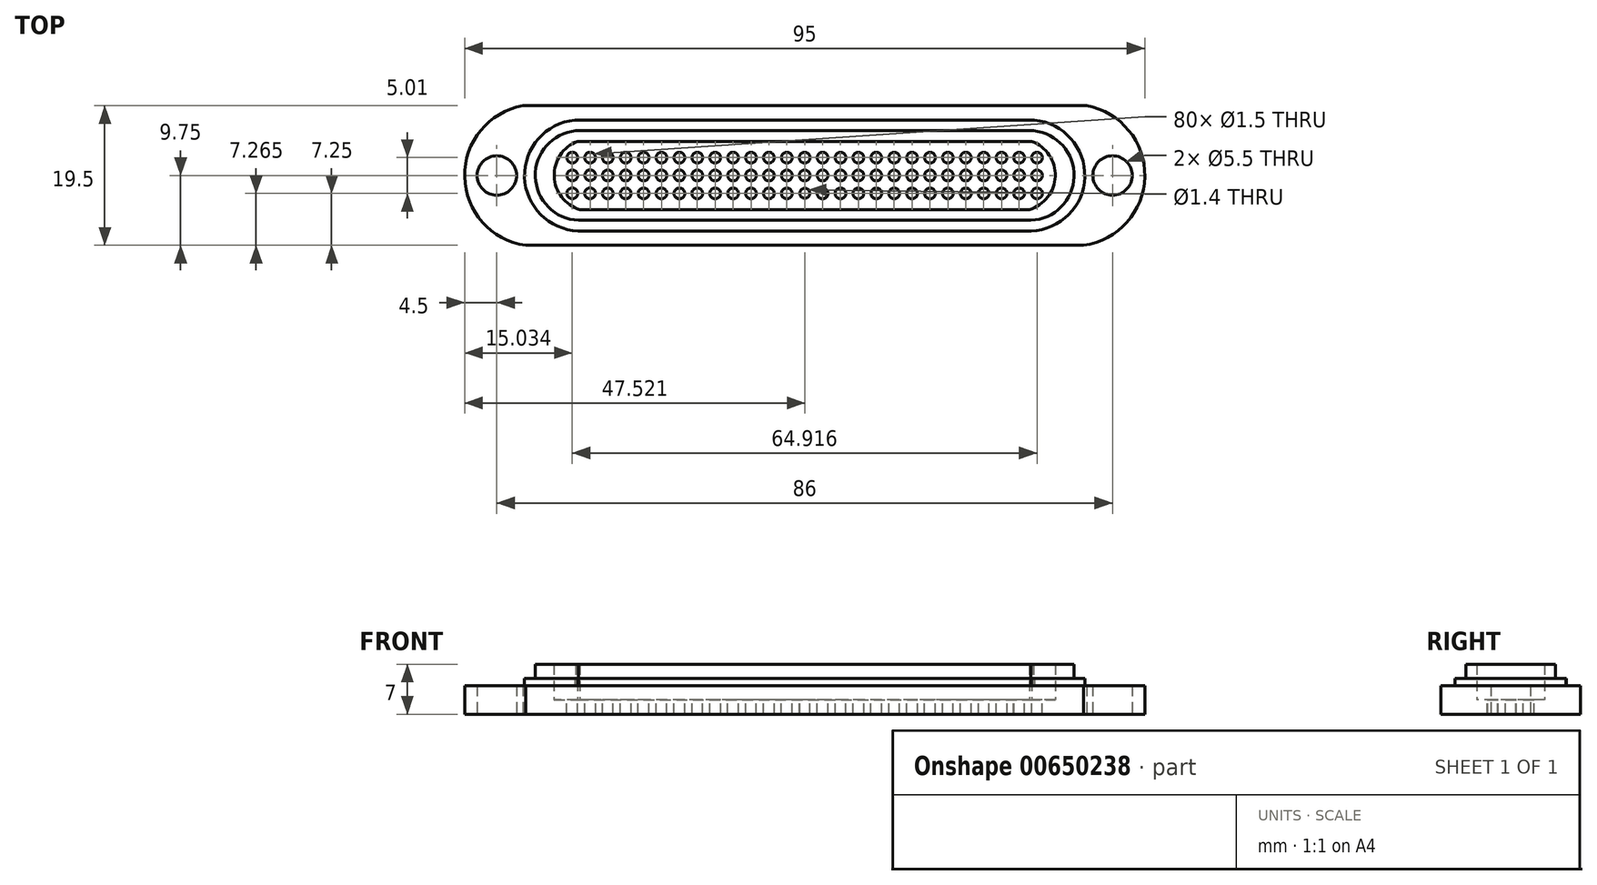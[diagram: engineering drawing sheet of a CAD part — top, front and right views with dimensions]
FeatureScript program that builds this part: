
annotation { "Feature Type Name" : "Feature", "Feature Type Description" : "" }
export const myFeature = defineFeature(function(context is Context, id is Id, definition is map)
    precondition{}
    {
        {
            var Q0;
            Q0=qCreatedBy(makeId("Top.planeOp"),FACE);
            var sketch = newSketch(context, id + "F0", { "sketchPlane" : qUnion([Q0])});
            skLineSegment(sketch, "E0.bottom", {"start": v(0, -9.75) * mm, "end": v(-38.98, -9.75) * mm});
            skLineSegment(sketch, "E0.top", {"start": v(0, 9.75) * mm, "end": v(-39.37, 9.75) * mm});
            skLineSegment(sketch, "E0.right", {"start": v(-47.5, 0) * mm, "end": v(-47.5, 0) * mm});
            skPoint(sketch, "E0.middle", {"position": v(0, 0) * mm});
            skArc(sketch, "E1", {"start": v(-39.37, 9.75) * mm, "mid": v(-47.5, -0.17) * mm, "end": v(-38.98, -9.75) * mm});
            skPoint(sketch, "E1.first.point", {"position": v(-38.98, -9.75) * mm});
            skPoint(sketch, "E1.second.point", {"position": v(-39.37, 9.75) * mm});
            skPoint(sketch, "E1.third.point", {"position": v(-47.5, 0) * mm});
            skLineSegment(sketch, "E2", {"start": v(0, 13.54) * mm, "end": v(0, -9.75) * mm, "construction": true});
            skPoint(sketch, "E3.orphan", {"position": v(-47.5, 9.75) * mm});
            skPoint(sketch, "E4.orphan", {"position": v(-47.5, -9.75) * mm});
            skPoint(sketch, "E0.left.end.orphan", {"position": v(47.5, 9.75) * mm});
            skPoint(sketch, "E0.left.start.orphan", {"position": v(47.5, -9.75) * mm});
            skLineSegment(sketch, "E5", {"start": v(-47.5, 0) * mm, "end": v(-43, 0) * mm, "construction": true});
            skCircle(sketch, "E6", {"center": v(-43, 0) * mm, "radius": 2.75 * mm});
            skLineSegment(sketch, "E7.MirrorCS", {"start": v(47.5, 0) * mm, "end": v(47.5, 0) * mm});
            skLineSegment(sketch, "E8.MirrorCS", {"start": v(47.5, 0) * mm, "end": v(43, 0) * mm, "construction": true});
            skPoint(sketch, "E9.MirrorP", {"position": v(39.37, 9.75) * mm});
            skArc(sketch, "E10.MirrorCS", {"start": v(39.37, 9.75) * mm, "mid": v(47.5, -0.17) * mm, "end": v(38.98, -9.75) * mm});
            skPoint(sketch, "E11.MirrorP", {"position": v(38.98, -9.75) * mm});
            skCircle(sketch, "E12.MirrorC", {"center": v(43, 0) * mm, "radius": 2.75 * mm});
            skPoint(sketch, "E13.MirrorP", {"position": v(47.5, 0) * mm});
            skLineSegment(sketch, "E14.MirrorCS", {"start": v(0, -9.75) * mm, "end": v(38.98, -9.75) * mm});
            skLineSegment(sketch, "E15.MirrorCS", {"start": v(0, 9.75) * mm, "end": v(39.37, 9.75) * mm});
            skLineSegment(sketch, "E16.0", {"start": v(-0.33, -6.25) * mm, "end": v(-31.59, -6.25) * mm});
            skLineSegment(sketch, "E16.2", {"start": v(-5.28, -6.25) * mm, "end": v(31.59, -6.25) * mm});
            skLineSegment(sketch, "E16.4", {"start": v(0, 6.25) * mm, "end": v(31.96, 6.25) * mm});
            skLineSegment(sketch, "E16.5", {"start": v(0, 6.25) * mm, "end": v(-31.96, 6.25) * mm});
            skLineSegment(sketch, "E17.0", {"start": v(-0.33, -4.75) * mm, "end": v(-31.39, -4.75) * mm});
            skArc(sketch, "E17.1", {"start": v(-31.71, 4.75) * mm, "mid": v(-35, -0.12) * mm, "end": v(-31.39, -4.75) * mm});
            skLineSegment(sketch, "E17.2", {"start": v(-5.28, -4.75) * mm, "end": v(31.39, -4.75) * mm});
            skArc(sketch, "E17.3", {"start": v(31.71, 4.75) * mm, "mid": v(35, -0.12) * mm, "end": v(31.39, -4.75) * mm});
            skLineSegment(sketch, "E17.4", {"start": v(0, 4.75) * mm, "end": v(31.71, 4.75) * mm});
            skLineSegment(sketch, "E17.5", {"start": v(0, 4.75) * mm, "end": v(-31.71, 4.75) * mm});
            skLineSegment(sketch, "E18", {"start": v(-0.33, -4.75) * mm, "end": v(-5.28, -4.75) * mm});
            skLineSegment(sketch, "E19", {"start": v(-5.28, -6.25) * mm, "end": v(-0.33, -6.25) * mm});
            skArc(sketch, "E20", {"start": v(-31.96, 6.25) * mm, "mid": v(-37.62, -0.17) * mm, "end": v(-31.59, -6.25) * mm});
            skArc(sketch, "E21", {"start": v(31.59, -6.25) * mm, "mid": v(37.62, -0.18) * mm, "end": v(31.96, 6.25) * mm});
            skArc(sketch, "E22.0", {"start": v(-32.1, 7.74) * mm, "mid": v(-39.12, -0.22) * mm, "end": v(-31.64, -7.75) * mm});
            skLineSegment(sketch, "E23.0", {"start": v(0, 7.75) * mm, "end": v(-31.96, 7.75) * mm});
            skLineSegment(sketch, "E24.0", {"start": v(-0.33, -7.75) * mm, "end": v(-31.59, -7.75) * mm});
            skLineSegment(sketch, "E25.MirrorCS", {"start": v(0, 7.75) * mm, "end": v(31.96, 7.75) * mm});
            skArc(sketch, "E26.MirrorCS", {"start": v(32.1, 7.74) * mm, "mid": v(39.12, -0.22) * mm, "end": v(31.64, -7.75) * mm});
            skLineSegment(sketch, "E27.MirrorCS", {"start": v(0.33, -7.75) * mm, "end": v(31.59, -7.75) * mm});
            skLineSegment(sketch, "E28", {"start": v(-0.33, -7.75) * mm, "end": v(0.33, -7.75) * mm});
            skLineSegment(sketch, "E29", {"start": v(-32.1, 7.74) * mm, "end": v(-31.96, 7.75) * mm});
            skLineSegment(sketch, "E30", {"start": v(-31.64, -7.75) * mm, "end": v(-31.59, -7.75) * mm});
            skLineSegment(sketch, "E31", {"start": v(31.59, -7.75) * mm, "end": v(31.64, -7.75) * mm});
            skLineSegment(sketch, "E32", {"start": v(31.96, 7.75) * mm, "end": v(32.1, 7.74) * mm});
            skSolve(sketch);
        }
        {
            var Q0;
            Q0 = qSketchRegion(id + "F0", true);
            extrude(context, id + "F1", {"entities" : qUnion([Q0]), "depth" : 4 * mm, "offsetDistance" : 25 * mm});
        }
        {
            var Q0;
            Q0=makeQuery(id+"F0.imprint","IMPRINT",FACE,{"disambiguationData":[TD([[makeQuery(id+"F0.imprint","IMPRINT",EDGE,{"derivedFrom":sQuery(id+"F0.wireOp",EDGE,"E16.0")}),1.0]])]});
            extrude(context, id + "F2", {"entities" : qUnion([Q0]), "operationType" : NewBodyOperationType.ADD, "depth" : 5 * mm, "offsetDistance" : 25 * mm});
        }
        {
            var Q0;
            Q0=makeQuery(id+"F0.imprint","IMPRINT",FACE,{"disambiguationData":[TD([[makeQuery(id+"F0.imprint","IMPRINT",EDGE,{"derivedFrom":sQuery(id+"F0.wireOp",EDGE,"E16.0")}),-1.0]])]});
            extrude(context, id + "F3", {"entities" : qUnion([Q0]), "operationType" : NewBodyOperationType.ADD, "depth" : 7 * mm, "offsetDistance" : 25 * mm});
        }
        {
            var Q0;
            Q0=makeQuery(id+"F0.imprint","IMPRINT",FACE,{"disambiguationData":[TD([[makeQuery(id+"F0.imprint","IMPRINT",EDGE,{"derivedFrom":sQuery(id+"F0.wireOp",EDGE,"E17.0")}),-1.0]])]});
            extrude(context, id + "F4", {"entities" : qUnion([Q0]), "operationType" : NewBodyOperationType.ADD, "depth" : 2 * mm, "offsetDistance" : 25 * mm});
        }
        {
            var Q0;
            Q0=makeQuery(id+"F4.opExtrude","CAP_FACE",FACE,{"disambiguationData":[OSD([sQuery(id+"F0.wireOp",EDGE,"E17.0"),sQuery(id+"F0.wireOp",EDGE,"E17.1"),sQuery(id+"F0.wireOp",EDGE,"E17.2"),sQuery(id+"F0.wireOp",EDGE,"E17.3"),sQuery(id+"F0.wireOp",EDGE,"E17.4"),sQuery(id+"F0.wireOp",EDGE,"E17.5"),sQuery(id+"F0.wireOp",EDGE,"E18")])],"isStart":false});
            var sketch = newSketch(context, id + "F5", { "sketchPlane" : qUnion([Q0])});
            skArc(sketch, "E33", {"start": v(0, -0.75) * mm, "mid": v(0.75, 0) * mm, "end": v(0, 0.75) * mm});
            skArc(sketch, "E34.0.1.0", {"start": v(0, 1.75) * mm, "mid": v(0.75, 2.5) * mm, "end": v(0, 3.25) * mm});
            skCircle(sketch, "E34.1.0.0", {"center": v(2.5, 0) * mm, "radius": 0.75 * mm});
            skCircle(sketch, "E34.1.1.0", {"center": v(2.5, 2.5) * mm, "radius": 0.75 * mm});
            skCircle(sketch, "E34.2.0.0", {"center": v(5, 0) * mm, "radius": 0.75 * mm});
            skCircle(sketch, "E34.2.1.0", {"center": v(5, 2.5) * mm, "radius": 0.75 * mm});
            skCircle(sketch, "E34.3.0.0", {"center": v(7.5, 0) * mm, "radius": 0.75 * mm});
            skCircle(sketch, "E34.3.1.0", {"center": v(7.5, 2.5) * mm, "radius": 0.75 * mm});
            skCircle(sketch, "E34.4.0.0", {"center": v(10, 0) * mm, "radius": 0.75 * mm});
            skCircle(sketch, "E34.4.1.0", {"center": v(10, 2.5) * mm, "radius": 0.75 * mm});
            skCircle(sketch, "E34.5.0.0", {"center": v(12.5, 0) * mm, "radius": 0.75 * mm});
            skCircle(sketch, "E34.5.1.0", {"center": v(12.5, 2.5) * mm, "radius": 0.75 * mm});
            skCircle(sketch, "E34.6.0.0", {"center": v(15, 0) * mm, "radius": 0.75 * mm});
            skCircle(sketch, "E34.6.1.0", {"center": v(15, 2.5) * mm, "radius": 0.75 * mm});
            skCircle(sketch, "E34.7.0.0", {"center": v(17.5, 0) * mm, "radius": 0.75 * mm});
            skCircle(sketch, "E34.7.1.0", {"center": v(17.5, 2.5) * mm, "radius": 0.75 * mm});
            skCircle(sketch, "E34.8.0.0", {"center": v(20, 0) * mm, "radius": 0.75 * mm});
            skCircle(sketch, "E34.8.1.0", {"center": v(20, 2.5) * mm, "radius": 0.75 * mm});
            skCircle(sketch, "E34.9.0.0", {"center": v(22.5, 0) * mm, "radius": 0.75 * mm});
            skCircle(sketch, "E34.9.1.0", {"center": v(22.5, 2.5) * mm, "radius": 0.75 * mm});
            skCircle(sketch, "E34.10.0.0", {"center": v(25, 0) * mm, "radius": 0.75 * mm});
            skCircle(sketch, "E34.10.1.0", {"center": v(25, 2.5) * mm, "radius": 0.75 * mm});
            skCircle(sketch, "E34.11.0.0", {"center": v(27.5, 0) * mm, "radius": 0.75 * mm});
            skCircle(sketch, "E34.11.1.0", {"center": v(27.5, 2.5) * mm, "radius": 0.75 * mm});
            skLineSegment(sketch, "E34.direction1", {"start": v(0, 0) * mm, "end": v(2.5, 0) * mm, "construction": true});
            skLineSegment(sketch, "E34.direction2", {"start": v(0, 0) * mm, "end": v(0, 2.5) * mm, "construction": true});
            skLineSegment(sketch, "E35", {"start": v(0, 4) * mm, "end": v(0, -4) * mm, "construction": true});
            skCircle(sketch, "E36.0.1.0", {"center": v(2.5, -2.5) * mm, "radius": 0.75 * mm});
            skCircle(sketch, "E36.1.1.0", {"center": v(5, -2.5) * mm, "radius": 0.75 * mm});
            skCircle(sketch, "E36.2.1.0", {"center": v(7.5, -2.5) * mm, "radius": 0.75 * mm});
            skCircle(sketch, "E36.3.1.0", {"center": v(10, -2.5) * mm, "radius": 0.75 * mm});
            skCircle(sketch, "E36.4.1.0", {"center": v(12.5, -2.5) * mm, "radius": 0.75 * mm});
            skCircle(sketch, "E36.5.1.0", {"center": v(15, -2.5) * mm, "radius": 0.75 * mm});
            skCircle(sketch, "E36.6.1.0", {"center": v(17.5, -2.5) * mm, "radius": 0.75 * mm});
            skCircle(sketch, "E36.7.1.0", {"center": v(20, -2.5) * mm, "radius": 0.75 * mm});
            skCircle(sketch, "E36.8.1.0", {"center": v(22.5, -2.5) * mm, "radius": 0.75 * mm});
            skCircle(sketch, "E36.9.1.0", {"center": v(25, -2.5) * mm, "radius": 0.75 * mm});
            skCircle(sketch, "E36.10.1.0", {"center": v(27.5, -2.5) * mm, "radius": 0.75 * mm});
            skLineSegment(sketch, "E36.direction1", {"start": v(2.5, 0) * mm, "end": v(5, 0) * mm, "construction": true});
            skLineSegment(sketch, "E36.direction2", {"start": v(2.5, 0) * mm, "end": v(2.5, -2.5) * mm, "construction": true});
            skArc(sketch, "E37.MirrorCS", {"start": v(0, 1.75) * mm, "mid": v(-0.75, 2.5) * mm, "end": v(0, 3.25) * mm});
            skCircle(sketch, "E38.MirrorC", {"center": v(-12.5, 0) * mm, "radius": 0.75 * mm});
            skCircle(sketch, "E39.MirrorC", {"center": v(-17.5, 0) * mm, "radius": 0.75 * mm});
            skCircle(sketch, "E40.MirrorC", {"center": v(-7.5, 0) * mm, "radius": 0.75 * mm});
            skCircle(sketch, "E41.MirrorC", {"center": v(-5, 0) * mm, "radius": 0.75 * mm});
            skCircle(sketch, "E42.MirrorC", {"center": v(-15, 0) * mm, "radius": 0.75 * mm});
            skCircle(sketch, "E43.MirrorC", {"center": v(-20, 0) * mm, "radius": 0.75 * mm});
            skCircle(sketch, "E44.MirrorC", {"center": v(-10, 0) * mm, "radius": 0.75 * mm});
            skCircle(sketch, "E45.MirrorC", {"center": v(-12.5, 2.5) * mm, "radius": 0.75 * mm});
            skCircle(sketch, "E46.MirrorC", {"center": v(-10, 2.5) * mm, "radius": 0.75 * mm});
            skCircle(sketch, "E47.MirrorC", {"center": v(-7.5, 2.5) * mm, "radius": 0.75 * mm});
            skCircle(sketch, "E48.MirrorC", {"center": v(-5, 2.5) * mm, "radius": 0.75 * mm});
            skCircle(sketch, "E49.MirrorC", {"center": v(-2.5, 0) * mm, "radius": 0.75 * mm});
            skCircle(sketch, "E50.MirrorC", {"center": v(-2.5, 2.5) * mm, "radius": 0.75 * mm});
            skArc(sketch, "E51.MirrorCS", {"start": v(0, -0.75) * mm, "mid": v(-0.75, 0) * mm, "end": v(0, 0.75) * mm});
            skCircle(sketch, "E52.MirrorC", {"center": v(-17.5, 2.5) * mm, "radius": 0.75 * mm});
            skCircle(sketch, "E53.MirrorC", {"center": v(-15, 2.5) * mm, "radius": 0.75 * mm});
            skLineSegment(sketch, "E54.MirrorCS", {"start": v(0, 0) * mm, "end": v(-2.5, 0) * mm, "construction": true});
            skCircle(sketch, "E55.MirrorC", {"center": v(-20, 2.5) * mm, "radius": 0.75 * mm});
            skLineSegment(sketch, "E56.MirrorCS", {"start": v(-2.5, 0) * mm, "end": v(-2.5, -2.5) * mm, "construction": true});
            skLineSegment(sketch, "E57.MirrorCS", {"start": v(-2.5, 0) * mm, "end": v(-5, 0) * mm, "construction": true});
            skCircle(sketch, "E58.MirrorC", {"center": v(-27.5, 0) * mm, "radius": 0.75 * mm});
            skCircle(sketch, "E59.MirrorC", {"center": v(-22.5, 0) * mm, "radius": 0.75 * mm});
            skCircle(sketch, "E60.MirrorC", {"center": v(-25, 0) * mm, "radius": 0.75 * mm});
            skCircle(sketch, "E61.MirrorC", {"center": v(-27.5, -2.5) * mm, "radius": 0.75 * mm});
            skCircle(sketch, "E62.MirrorC", {"center": v(-25, 2.5) * mm, "radius": 0.75 * mm});
            skCircle(sketch, "E63.MirrorC", {"center": v(-22.5, 2.5) * mm, "radius": 0.75 * mm});
            skCircle(sketch, "E64.MirrorC", {"center": v(-17.5, -2.5) * mm, "radius": 0.75 * mm});
            skCircle(sketch, "E65.MirrorC", {"center": v(-27.5, 2.5) * mm, "radius": 0.75 * mm});
            skCircle(sketch, "E66.MirrorC", {"center": v(-20, -2.5) * mm, "radius": 0.75 * mm});
            skCircle(sketch, "E67.MirrorC", {"center": v(-22.5, -2.5) * mm, "radius": 0.75 * mm});
            skCircle(sketch, "E68.MirrorC", {"center": v(-25, -2.5) * mm, "radius": 0.75 * mm});
            skCircle(sketch, "E69.MirrorC", {"center": v(-2.5, -2.5) * mm, "radius": 0.75 * mm});
            skCircle(sketch, "E70.MirrorC", {"center": v(-5, -2.5) * mm, "radius": 0.75 * mm});
            skCircle(sketch, "E71.MirrorC", {"center": v(-7.5, -2.5) * mm, "radius": 0.75 * mm});
            skCircle(sketch, "E72.MirrorC", {"center": v(-10, -2.5) * mm, "radius": 0.75 * mm});
            skCircle(sketch, "E73.MirrorC", {"center": v(-12.5, -2.5) * mm, "radius": 0.75 * mm});
            skCircle(sketch, "E74.MirrorC", {"center": v(-15, -2.5) * mm, "radius": 0.75 * mm});
            skCircle(sketch, "E75.0.1.0", {"center": v(0.02, -2.49) * mm, "radius": 0.7 * mm});
            skLineSegment(sketch, "E76", {"start": v(-27.5, 0) * mm, "end": v(-30, 0) * mm, "construction": true});
            skCircle(sketch, "E77.MirrorC", {"center": v(-29.96, 0.04) * mm, "radius": 0.75 * mm});
            skCircle(sketch, "E78.MirrorC", {"center": v(29.96, 0.04) * mm, "radius": 0.75 * mm});
            skCircle(sketch, "E79.9.1.0", {"center": v(29.95, 2.5) * mm, "radius": 0.75 * mm});
            skCircle(sketch, "E79.10.1.0", {"center": v(32.45, 2.5) * mm, "radius": 0.75 * mm});
            skCircle(sketch, "E80.8.1.0", {"center": v(29.95, -2.5) * mm, "radius": 0.75 * mm});
            skCircle(sketch, "E80.9.0.0", {"center": v(32.45, 0) * mm, "radius": 0.75 * mm});
            skCircle(sketch, "E80.9.1.0", {"center": v(32.45, -2.5) * mm, "radius": 0.75 * mm});
            skCircle(sketch, "E81.MirrorC", {"center": v(-32.47, 0) * mm, "radius": 0.75 * mm});
            skCircle(sketch, "E82.MirrorC", {"center": v(-32.47, -2.5) * mm, "radius": 0.75 * mm});
            skCircle(sketch, "E83.MirrorC", {"center": v(-29.97, 2.5) * mm, "radius": 0.75 * mm});
            skCircle(sketch, "E84.MirrorC", {"center": v(-32.47, 2.5) * mm, "radius": 0.75 * mm});
            skCircle(sketch, "E85.MirrorC", {"center": v(-29.97, -2.5) * mm, "radius": 0.75 * mm});
            skSolve(sketch);
        }
        {
            var Q0;
            Q0=qSketchRegion(id+"F5",true);
            extrude(context, id + "F6", {"entities" : qUnion([Q0]), "operationType" : NewBodyOperationType.REMOVE, "oppositeDirection" : true, "depth" : 25 * mm, "offsetDistance" : 25 * mm});
        }
    });
